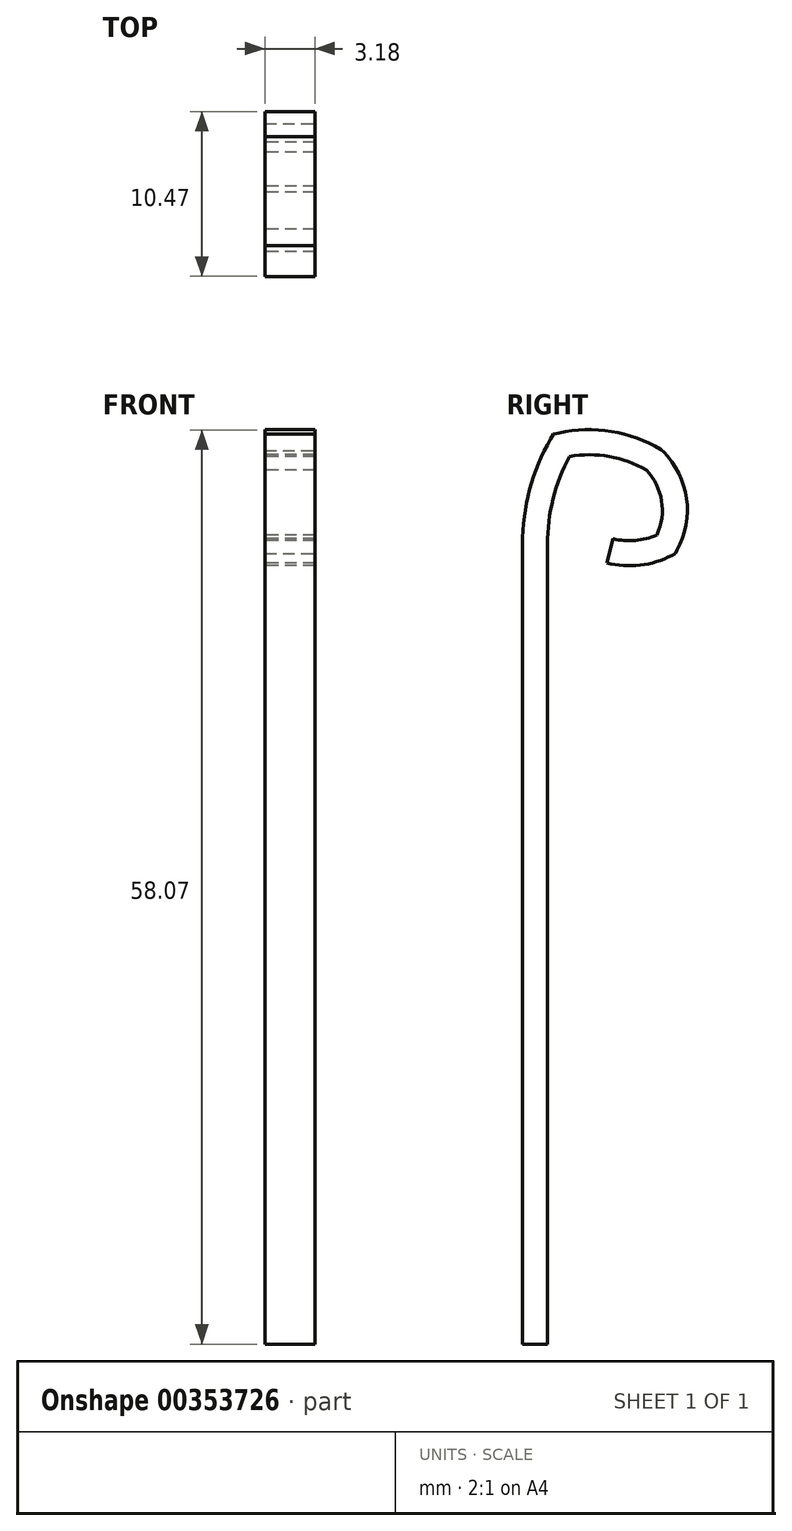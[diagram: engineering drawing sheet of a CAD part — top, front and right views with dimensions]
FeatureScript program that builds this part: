
annotation { "Feature Type Name" : "Feature", "Feature Type Description" : "" }
export const myFeature = defineFeature(function(context is Context, id is Id, definition is map)
    precondition{}
    {
        {
            var Q0;
            Q0=qCreatedBy(makeId("Top.planeOp"),FACE);
            var sketch = newSketch(context, id + "F0", { "sketchPlane" : qUnion([Q0])});
            skLineSegment(sketch, "E0.bottom", {"start": v(1.59, 0.8) * mm, "end": v(-1.59, 0.8) * mm});
            skLineSegment(sketch, "E0.top", {"start": v(1.59, -0.8) * mm, "end": v(-1.59, -0.8) * mm});
            skLineSegment(sketch, "E0.left", {"start": v(1.59, 0.8) * mm, "end": v(1.59, -0.8) * mm});
            skLineSegment(sketch, "E0.right", {"start": v(-1.59, 0.8) * mm, "end": v(-1.59, -0.8) * mm});
            skPoint(sketch, "E0.middle", {"position": v(0, 0) * mm});
            skSolve(sketch);
        }
        {
            var Q0;
            Q0=qCreatedBy(makeId("Right.planeOp"),FACE);
            var sketch = newSketch(context, id + "F1", { "sketchPlane" : qUnion([Q0])});
            skLineSegment(sketch, "E1", {"start": v(0, 0) * mm, "end": v(0, 50.8) * mm});
            skPoint(sketch, "E2.start.orphan", {"position": v(4.27, 50.8) * mm});
            skArc(sketch, "E3", {"start": v(8.33, 50.8) * mm, "mid": v(8.84, 53.6) * mm, "end": v(7.58, 56.14) * mm});
            skArc(sketch, "E4", {"start": v(4.76, 50.39) * mm, "mid": v(6.58, 50.26) * mm, "end": v(8.33, 50.8) * mm});
            skArc(sketch, "E5", {"start": v(1.68, 57.09) * mm, "mid": v(0.43, 54.05) * mm, "end": v(0, 50.8) * mm});
            skPoint(sketch, "E6.end.orphan", {"position": v(1.93, 56.14) * mm});
            skArc(sketch, "E7", {"start": v(7.58, 56.14) * mm, "mid": v(4.72, 57.18) * mm, "end": v(1.68, 57.09) * mm});
            skSolve(sketch);
        }
        {
            var Q0;
            Q0 = qSketchRegion(id + "F0", true);
            var Q1;
            Q1 = qConstructionFilter(qBodyType(qCreatedBy(id + "F1" ,EDGE), BodyType.WIRE), ConstructionObject.NO);
            sweep(context, id + "F2", {"profiles" : qUnion([Q0]), "path" : qUnion([Q1])});
        }
    });
